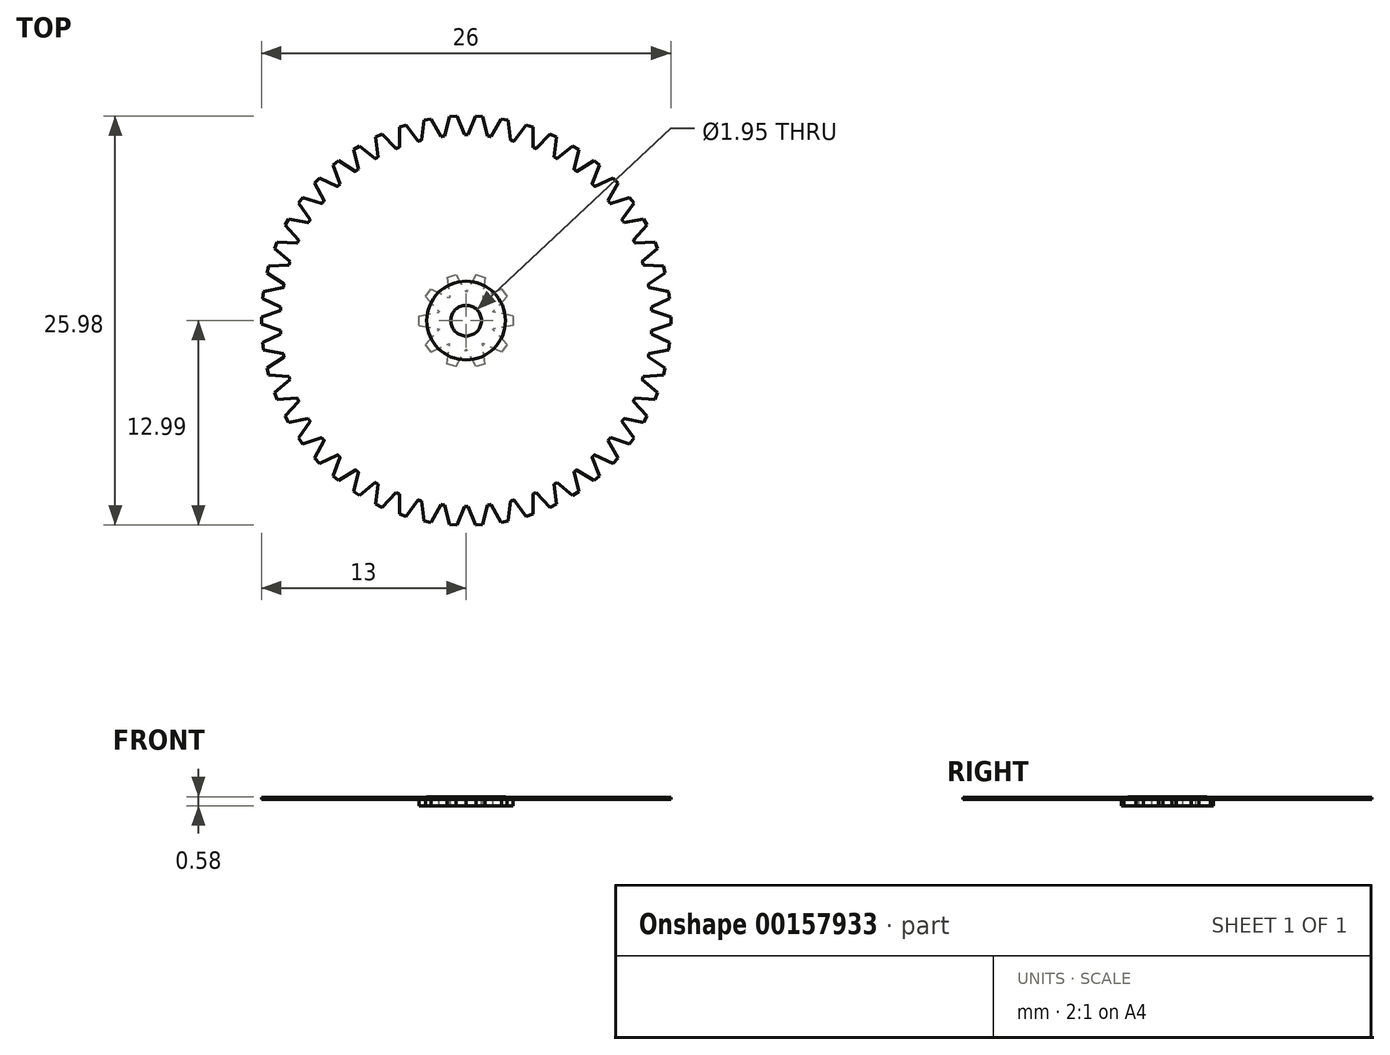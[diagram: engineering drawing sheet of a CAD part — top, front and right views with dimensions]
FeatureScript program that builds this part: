
annotation { "Feature Type Name" : "Feature", "Feature Type Description" : "" }
export const myFeature = defineFeature(function(context is Context, id is Id, definition is map)
    precondition{}
    {
        {
            var Q0;
            Q0=qCreatedBy(makeId("Front.planeOp"),FACE);
            var sketch = newSketch(context, id + "F0", { "sketchPlane" : qUnion([Q0])});
            skLineSegment(sketch, "E0", {"start": v(0, 0) * mm, "end": v(0, 40.99) * mm, "construction": true});
            skSolve(sketch);
        }
        {
            assignVariable(context, id + "F1", {"name" : "config", "anyValue" : 0});
        }
        {
            assignVariable(context, id + "F2", {"name" : "H1", "anyValue" : [0.15, 0.15][getVariable(context, 'config')]});
        }
        {
            assignVariable(context, id + "F3", {"name" : "H2", "anyValue" : [0.4, 0.4][getVariable(context, 'config')]});
        }
        {
            assignVariable(context, id + "F4", {"name" : "H3", "anyValue" : [0.03, 0.02][getVariable(context, 'config')]});
        }
        {
            assignVariable(context, id + "F5", {"name" : "N1", "anyValue" : [50, 40][getVariable(context, 'config')]});
        }
        {
            assignVariable(context, id + "F6", {"name" : "N2", "anyValue" : [10, 10][getVariable(context, 'config')]});
        }
        {
            var Q0;
            Q0=qCreatedBy(makeId("Top.planeOp"),FACE);
            var sketch = newSketch(context, id + "F7", { "sketchPlane" : qUnion([Q0])});
            skCircle(sketch, "E1", {"center": v(0, 0) * mm, "radius": 13 * mm, "construction": true});
            skCircle(sketch, "E2", {"center": v(0, 0) * mm, "radius": 11.8 * mm});
            skCircle(sketch, "E3", {"center": v(0, 0) * mm, "radius": 12.5 * mm, "construction": true});
            skLineSegment(sketch, "E4", {"start": v(0, 0) * mm, "end": v(0, 11.8) * mm});
            skLineSegment(sketch, "E5", {"start": v(0, 0) * mm, "end": v(1.48, 11.7) * mm});
            skLineSegment(sketch, "E6", {"start": v(0.82, 12.97) * mm, "end": v(0, 0) * mm, "construction": true});
            skLineSegment(sketch, "E7", {"start": v(0.4, 12.5) * mm, "end": v(1.18, 12.45) * mm, "construction": true});
            skPoint(sketch, "E8", {"position": v(0.78, 12.48) * mm});
            skLineSegment(sketch, "E9", {"start": v(0, 0) * mm, "end": v(0.4, 13) * mm, "construction": true});
            skLineSegment(sketch, "E10", {"start": v(0.59, 12.99) * mm, "end": v(0.11, 11.8) * mm});
            skLineSegment(sketch, "E11.MirrorCS", {"start": v(1.04, 12.96) * mm, "end": v(1.37, 11.72) * mm});
            skLineSegment(sketch, "E12", {"start": v(0.59, 12.99) * mm, "end": v(1.04, 12.96) * mm});
            skLineSegment(sketch, "E13", {"start": v(-2.34, 12.58) * mm, "end": v(4.03, 12.38) * mm, "construction": true});
            skPoint(sketch, "E14", {"position": v(0.4, 12.5) * mm});
            skLineSegment(sketch, "E15", {"start": v(0.4, 12.5) * mm, "end": v(-0.1, 12.69) * mm, "construction": true});
            skSolve(sketch);
        }
        {
            var Q0;
            Q0=qCreatedBy(makeId("Top.planeOp"),FACE);
            var sketch = newSketch(context, id + "F8", { "sketchPlane" : qUnion([Q0])});
            skCircle(sketch, "E16", {"center": v(0, 0) * mm, "radius": 3 * mm, "construction": true});
            skCircle(sketch, "E17", {"center": v(0, 0) * mm, "radius": 1.8 * mm});
            skCircle(sketch, "E18", {"center": v(0, 0) * mm, "radius": 2.5 * mm, "construction": true});
            skLineSegment(sketch, "E19", {"start": v(0, 0) * mm, "end": v(0, 1.8) * mm});
            skLineSegment(sketch, "E20", {"start": v(0, 0) * mm, "end": v(1.06, 1.46) * mm});
            skLineSegment(sketch, "E21", {"start": v(0.93, 2.85) * mm, "end": v(0, 0) * mm, "construction": true});
            skLineSegment(sketch, "E22", {"start": v(0.4, 2.5) * mm, "end": v(1.15, 2.26) * mm, "construction": true});
            skPoint(sketch, "E23", {"position": v(0.77, 2.38) * mm});
            skLineSegment(sketch, "E24", {"start": v(0, 0) * mm, "end": v(0.47, 2.96) * mm, "construction": true});
            skLineSegment(sketch, "E25", {"start": v(0.64, 2.93) * mm, "end": v(0.01, 1.8) * mm});
            skLineSegment(sketch, "E26.MirrorCS", {"start": v(1.2, 2.75) * mm, "end": v(1.05, 1.46) * mm});
            skLineSegment(sketch, "E27", {"start": v(0.64, 2.93) * mm, "end": v(1.2, 2.75) * mm});
            skSolve(sketch);
        }
        {
            var Q0;
            {var subQ0=sQuery(id+"F7.wireOp",EDGE,"E10");Q0=makeQuery(id+"F7.imprint","IMPRINT",FACE,{"disambiguationData":[TD([[makeQuery(id+"F7.imprint","IMPRINT",EDGE,{"derivedFrom":subQ0}),1.0]])]});}
            var Q1;
            {var subQ0=sQuery(id+"F7.wireOp",EDGE,"E4");Q1=makeQuery(id+"F7.imprint","IMPRINT",FACE,{"disambiguationData":[TD([[makeQuery(id+"F7.imprint","IMPRINT",EDGE,{"derivedFrom":subQ0}),-1.0]])]});}
            extrude(context, id + "F9", {"entities" : qUnion([Q0, Q1]), "depth" : (getVariable(context, 'H1')) * mm});
        }
        {
            var Q0;
            Q0=makeQuery(id+"F9.opExtrude","SWEPT_BODY",BODY,{"disambiguationData":[OSD([sQuery(id+"F7.wireOp",EDGE,"E2"),sQuery(id+"F7.wireOp",EDGE,"E4"),sQuery(id+"F7.wireOp",EDGE,"E5"),sQuery(id+"F7.wireOp",EDGE,"E10"),sQuery(id+"F7.wireOp",EDGE,"E11.MirrorCS"),sQuery(id+"F7.wireOp",EDGE,"E12")])]});
            var Q1;
            Q1=sQuery(id+"F0.wireOp",EDGE,"E0");
            circularPattern(context, id + "F10", {"operationType" : NewBodyOperationType.ADD, "entities" : qUnion([Q0]), "axis" : qUnion([Q1]), "angle" : 360 * degree, "instanceCount" : getVariable(context, 'N1'), "equalSpace" : true});
        }
        {
            var Q0;
            {var subQ0=sQuery(id+"F8.wireOp",EDGE,"E19");Q0=makeQuery(id+"F8.imprint","IMPRINT",FACE,{"disambiguationData":[TD([[makeQuery(id+"F8.imprint","IMPRINT",EDGE,{"derivedFrom":subQ0}),-1.0]])]});}
            var Q1;
            {var subQ0=sQuery(id+"F8.wireOp",EDGE,"E25");Q1=makeQuery(id+"F8.imprint","IMPRINT",FACE,{"disambiguationData":[TD([[makeQuery(id+"F8.imprint","IMPRINT",EDGE,{"derivedFrom":subQ0}),1.0]])]});}
            extrude(context, id + "F11", {"entities" : qUnion([Q0, Q1]), "oppositeDirection" : true, "depth" : (getVariable(context, 'H2')) * mm});
        }
        {
            var Q0;
            Q0=makeQuery(id+"F11.opExtrude","SWEPT_BODY",BODY,{"disambiguationData":[OSD([sQuery(id+"F8.wireOp",EDGE,"E17"),sQuery(id+"F8.wireOp",EDGE,"E19"),sQuery(id+"F8.wireOp",EDGE,"E20"),sQuery(id+"F8.wireOp",EDGE,"E25"),sQuery(id+"F8.wireOp",EDGE,"E26.MirrorCS"),sQuery(id+"F8.wireOp",EDGE,"E27")])]});
            var Q1;
            Q1=sQuery(id+"F0.wireOp",EDGE,"E0");
            circularPattern(context, id + "F12", {"operationType" : NewBodyOperationType.ADD, "entities" : qUnion([Q0]), "axis" : qUnion([Q1]), "angle" : 360 * degree, "instanceCount" : getVariable(context, 'N2'), "equalSpace" : true});
        }
        {
            var Q0;
            Q0=qCreatedBy(makeId("Top.planeOp"),FACE);
            var sketch = newSketch(context, id + "F13", { "sketchPlane" : qUnion([Q0])});
            skCircle(sketch, "E28", {"center": v(0, 0) * mm, "radius": 0.98 * mm});
            skCircle(sketch, "E29", {"center": v(0, 0) * mm, "radius": 2.5 * mm});
            skSolve(sketch);
        }
        {
            var Q0;
            {var subQ0=makeQuery(id+"F9.opExtrude","CAP_FACE",FACE,{"disambiguationData":[OSD([sQuery(id+"F7.wireOp",EDGE,"E2"),sQuery(id+"F7.wireOp",EDGE,"E4"),sQuery(id+"F7.wireOp",EDGE,"E5"),sQuery(id+"F7.wireOp",EDGE,"E10"),sQuery(id+"F7.wireOp",EDGE,"E11.MirrorCS"),sQuery(id+"F7.wireOp",EDGE,"E12")])],"isStart":false});Q0=makeQuery(id+"F10.boolean.opBoolean","MERGE",FACE,{"derivedFrom":[subQ0,makeQuery(id+"F10.opPattern","COPY",FACE,{"derivedFrom":subQ0,"instanceName":"1"}),makeQuery(id+"F10.opPattern","COPY",FACE,{"derivedFrom":subQ0,"instanceName":"2"}),makeQuery(id+"F10.opPattern","COPY",FACE,{"derivedFrom":subQ0,"instanceName":"3"}),makeQuery(id+"F10.opPattern","COPY",FACE,{"derivedFrom":subQ0,"instanceName":"4"}),makeQuery(id+"F10.opPattern","COPY",FACE,{"derivedFrom":subQ0,"instanceName":"5"}),makeQuery(id+"F10.opPattern","COPY",FACE,{"derivedFrom":subQ0,"instanceName":"6"}),makeQuery(id+"F10.opPattern","COPY",FACE,{"derivedFrom":subQ0,"instanceName":"7"}),makeQuery(id+"F10.opPattern","COPY",FACE,{"derivedFrom":subQ0,"instanceName":"8"}),makeQuery(id+"F10.opPattern","COPY",FACE,{"derivedFrom":subQ0,"instanceName":"9"}),makeQuery(id+"F10.opPattern","COPY",FACE,{"derivedFrom":subQ0,"instanceName":"10"}),makeQuery(id+"F10.opPattern","COPY",FACE,{"derivedFrom":subQ0,"instanceName":"11"}),makeQuery(id+"F10.opPattern","COPY",FACE,{"derivedFrom":subQ0,"instanceName":"12"}),makeQuery(id+"F10.opPattern","COPY",FACE,{"derivedFrom":subQ0,"instanceName":"13"}),makeQuery(id+"F10.opPattern","COPY",FACE,{"derivedFrom":subQ0,"instanceName":"14"}),makeQuery(id+"F10.opPattern","COPY",FACE,{"derivedFrom":subQ0,"instanceName":"15"}),makeQuery(id+"F10.opPattern","COPY",FACE,{"derivedFrom":subQ0,"instanceName":"16"}),makeQuery(id+"F10.opPattern","COPY",FACE,{"derivedFrom":subQ0,"instanceName":"17"}),makeQuery(id+"F10.opPattern","COPY",FACE,{"derivedFrom":subQ0,"instanceName":"18"}),makeQuery(id+"F10.opPattern","COPY",FACE,{"derivedFrom":subQ0,"instanceName":"19"}),makeQuery(id+"F10.opPattern","COPY",FACE,{"derivedFrom":subQ0,"instanceName":"20"}),makeQuery(id+"F10.opPattern","COPY",FACE,{"derivedFrom":subQ0,"instanceName":"21"}),makeQuery(id+"F10.opPattern","COPY",FACE,{"derivedFrom":subQ0,"instanceName":"22"}),makeQuery(id+"F10.opPattern","COPY",FACE,{"derivedFrom":subQ0,"instanceName":"23"}),makeQuery(id+"F10.opPattern","COPY",FACE,{"derivedFrom":subQ0,"instanceName":"24"}),makeQuery(id+"F10.opPattern","COPY",FACE,{"derivedFrom":subQ0,"instanceName":"25"}),makeQuery(id+"F10.opPattern","COPY",FACE,{"derivedFrom":subQ0,"instanceName":"26"}),makeQuery(id+"F10.opPattern","COPY",FACE,{"derivedFrom":subQ0,"instanceName":"27"}),makeQuery(id+"F10.opPattern","COPY",FACE,{"derivedFrom":subQ0,"instanceName":"28"}),makeQuery(id+"F10.opPattern","COPY",FACE,{"derivedFrom":subQ0,"instanceName":"29"}),makeQuery(id+"F10.opPattern","COPY",FACE,{"derivedFrom":subQ0,"instanceName":"30"}),makeQuery(id+"F10.opPattern","COPY",FACE,{"derivedFrom":subQ0,"instanceName":"31"}),makeQuery(id+"F10.opPattern","COPY",FACE,{"derivedFrom":subQ0,"instanceName":"32"}),makeQuery(id+"F10.opPattern","COPY",FACE,{"derivedFrom":subQ0,"instanceName":"33"}),makeQuery(id+"F10.opPattern","COPY",FACE,{"derivedFrom":subQ0,"instanceName":"34"}),makeQuery(id+"F10.opPattern","COPY",FACE,{"derivedFrom":subQ0,"instanceName":"35"}),makeQuery(id+"F10.opPattern","COPY",FACE,{"derivedFrom":subQ0,"instanceName":"36"}),makeQuery(id+"F10.opPattern","COPY",FACE,{"derivedFrom":subQ0,"instanceName":"37"}),makeQuery(id+"F10.opPattern","COPY",FACE,{"derivedFrom":subQ0,"instanceName":"38"}),makeQuery(id+"F10.opPattern","COPY",FACE,{"derivedFrom":subQ0,"instanceName":"39"}),makeQuery(id+"F10.opPattern","COPY",FACE,{"derivedFrom":subQ0,"instanceName":"40"}),makeQuery(id+"F10.opPattern","COPY",FACE,{"derivedFrom":subQ0,"instanceName":"41"}),makeQuery(id+"F10.opPattern","COPY",FACE,{"derivedFrom":subQ0,"instanceName":"42"}),makeQuery(id+"F10.opPattern","COPY",FACE,{"derivedFrom":subQ0,"instanceName":"43"}),makeQuery(id+"F10.opPattern","COPY",FACE,{"derivedFrom":subQ0,"instanceName":"44"}),makeQuery(id+"F10.opPattern","COPY",FACE,{"derivedFrom":subQ0,"instanceName":"45"}),makeQuery(id+"F10.opPattern","COPY",FACE,{"derivedFrom":subQ0,"instanceName":"46"}),makeQuery(id+"F10.opPattern","COPY",FACE,{"derivedFrom":subQ0,"instanceName":"47"}),makeQuery(id+"F10.opPattern","COPY",FACE,{"derivedFrom":subQ0,"instanceName":"48"}),makeQuery(id+"F10.opPattern","COPY",FACE,{"derivedFrom":subQ0,"instanceName":"49"})]});}
            var sketch = newSketch(context, id + "F14", { "sketchPlane" : qUnion([Q0])});
            skCircle(sketch, "E30.0", {"center": v(0, 0) * mm, "radius": 2.5 * mm});
            skSolve(sketch);
        }
        {
            var Q0;
            Q0 = qSketchRegion(id + "F14", true);
            extrude(context, id + "F15", {"entities" : qUnion([Q0]), "operationType" : NewBodyOperationType.ADD, "depth" : (getVariable(context, 'H3')) * mm});
        }
        {
            var Q0;
            Q0=makeQuery(id+"F13.imprint","IMPRINT",FACE,{"disambiguationData":[TD([[makeQuery(id+"F13.imprint","IMPRINT",EDGE,{"derivedFrom":sQuery(id+"F13.wireOp",EDGE,"E28")}),1.0]])]});
            extrude(context, id + "F16", {"entities" : qUnion([Q0]), "operationType" : NewBodyOperationType.REMOVE, "endBound" : BoundingType.THROUGH_ALL, "oppositeDirection" : true, "depth" : 25 * mm, "hasSecondDirection" : true, "secondDirectionBound" : SecondDirectionBoundingType.THROUGH_ALL, "secondDirectionOppositeDirection" : false, "secondDirectionDepth" : 25 * mm});
        }
    });
